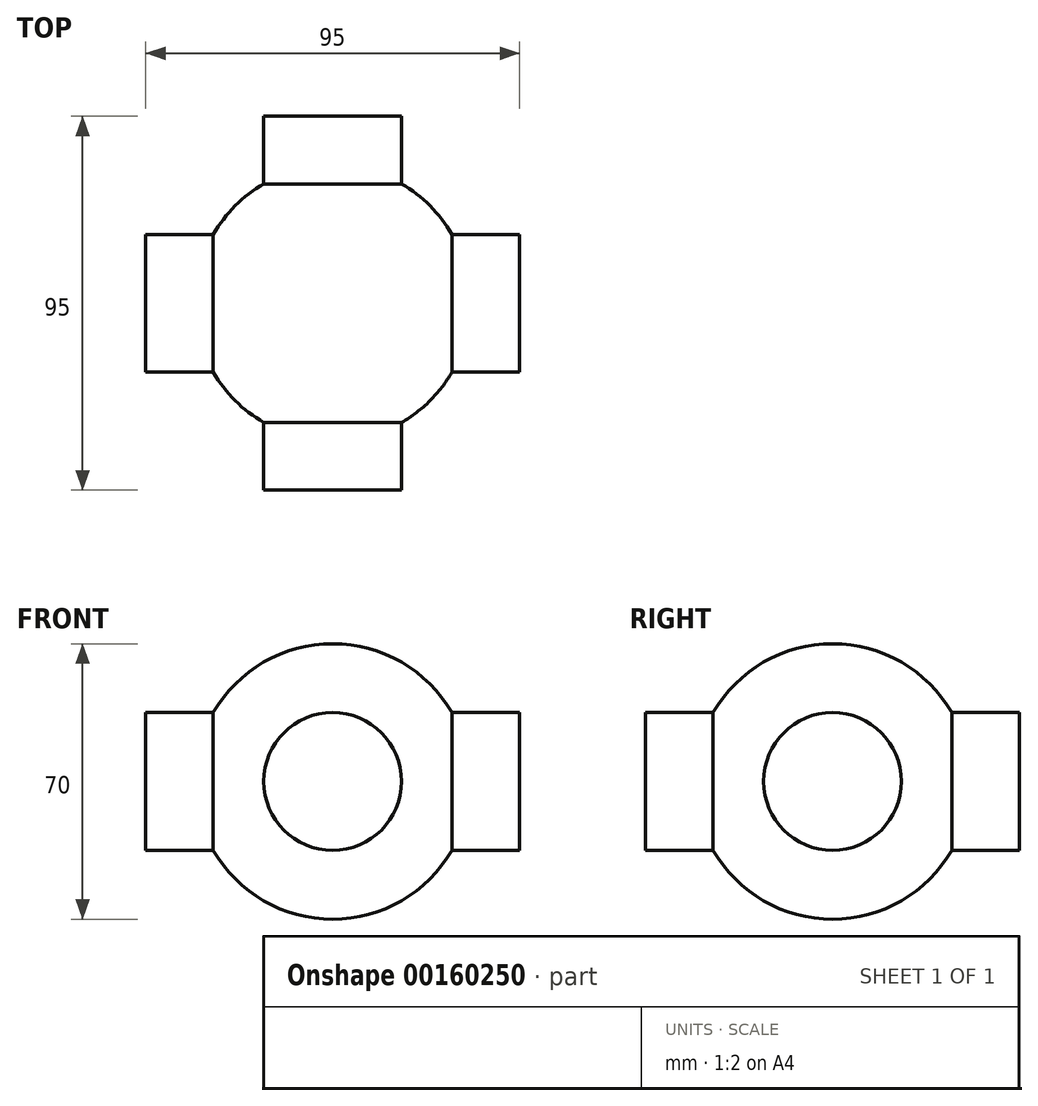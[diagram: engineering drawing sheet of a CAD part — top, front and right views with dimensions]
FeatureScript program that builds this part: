
annotation { "Feature Type Name" : "Feature", "Feature Type Description" : "" }
export const myFeature = defineFeature(function(context is Context, id is Id, definition is map)
    precondition{}
    {
        {
            var Q0;
            Q0=qCreatedBy(makeId("Front.planeOp"),FACE);
            var sketch = newSketch(context, id + "F0", { "sketchPlane" : qUnion([Q0])});
            skArc(sketch, "E0", {"start": v(0, 35) * mm, "mid": v(-35, 0) * mm, "end": v(0, -35) * mm});
            skLineSegment(sketch, "E1", {"start": v(0, 35) * mm, "end": v(0, -35) * mm});
            skSolve(sketch);
        }
        {
            var Q0;
            Q0=qSketchRegion(id+"F0",true);
            var Q1;
            Q1=sQuery(id+"F0.wireOp",EDGE,"E1");
            revolve(context, id + "F1", {"entities" : qUnion([Q0]), "axis" : qUnion([Q1]), "revolveType" : RevolveType.FULL});
        }
        {
            var Q0;
            Q0=qCreatedBy(makeId("Front.planeOp"),FACE);
            var sketch = newSketch(context, id + "F2", { "sketchPlane" : qUnion([Q0])});
            skCircle(sketch, "E2", {"center": v(0, 0) * mm, "radius": 17.5 * mm});
            skSolve(sketch);
        }
        {
            var Q0;
            Q0=qSketchRegion(id+"F2",true);
            extrude(context, id + "F3", {"entities" : qUnion([Q0]), "operationType" : NewBodyOperationType.ADD, "endBound" : BoundingType.SYMMETRIC, "depth" : 95 * mm});
        }
        {
            var Q0;
            Q0=qCreatedBy(makeId("Right.planeOp"),FACE);
            var sketch = newSketch(context, id + "F4", { "sketchPlane" : qUnion([Q0])});
            skCircle(sketch, "E3", {"center": v(0, 0) * mm, "radius": 17.5 * mm});
            skSolve(sketch);
        }
        {
            var Q0;
            Q0=qSketchRegion(id+"F4",true);
            extrude(context, id + "F5", {"entities" : qUnion([Q0]), "operationType" : NewBodyOperationType.ADD, "endBound" : BoundingType.SYMMETRIC, "depth" : 95 * mm});
        }
    });
